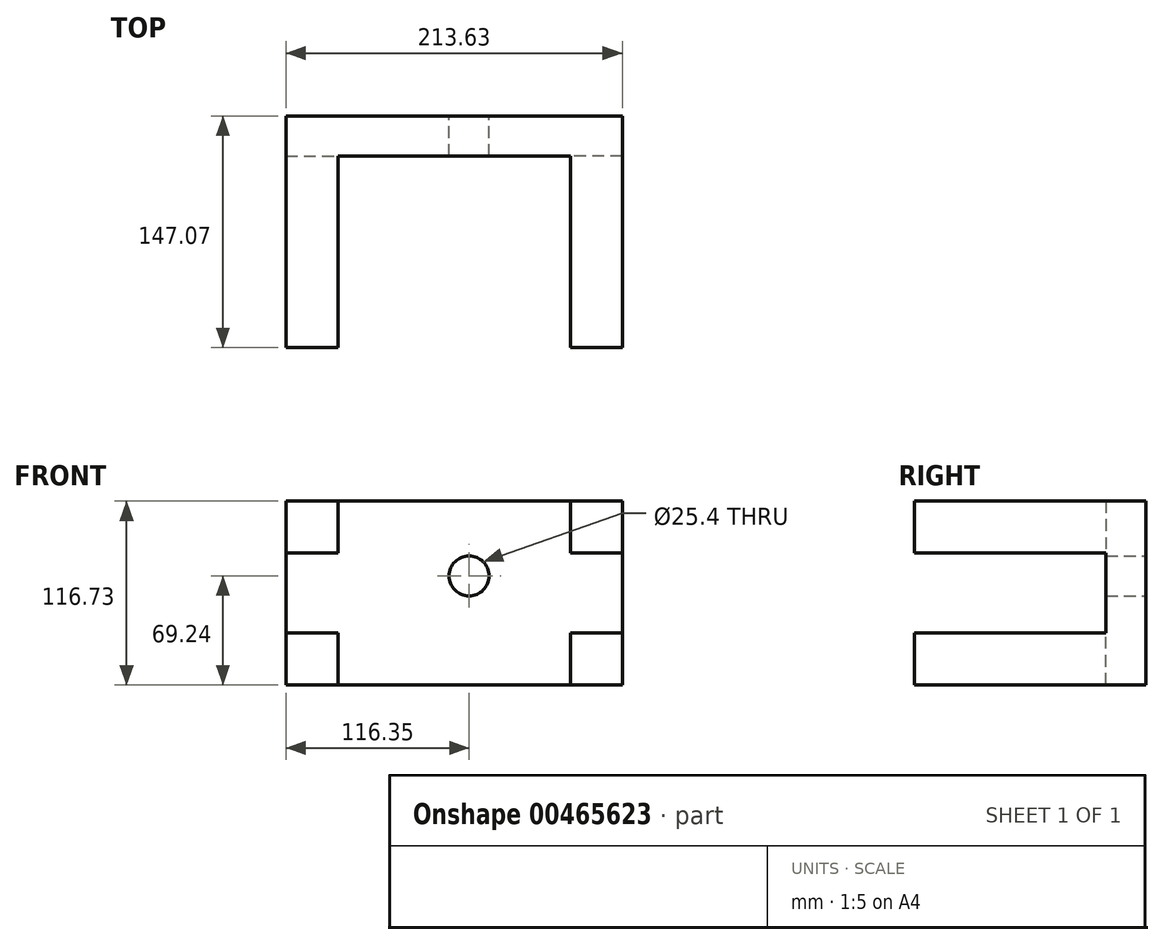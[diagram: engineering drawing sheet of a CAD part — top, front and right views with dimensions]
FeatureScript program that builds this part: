
annotation { "Feature Type Name" : "Feature", "Feature Type Description" : "" }
export const myFeature = defineFeature(function(context is Context, id is Id, definition is map)
    precondition{}
    {
        {
            var Q0;
            Q0=qCreatedBy(makeId("Front.planeOp"),FACE);
            var sketch = newSketch(context, id + "F0", { "sketchPlane" : qUnion([Q0])});
            skLineSegment(sketch, "E0.bottom", {"start": v(-116.35, 47.5) * mm, "end": v(97.28, 47.5) * mm});
            skLineSegment(sketch, "E0.top", {"start": v(-116.35, -69.24) * mm, "end": v(97.28, -69.24) * mm});
            skLineSegment(sketch, "E0.left", {"start": v(-116.35, 47.5) * mm, "end": v(-116.35, -69.24) * mm});
            skLineSegment(sketch, "E0.right", {"start": v(97.28, 47.5) * mm, "end": v(97.28, -69.24) * mm});
            skSolve(sketch);
        }
        {
            var Q0;
            Q0 = qSketchRegion(id + "F0", true);
            extrude(context, id + "F1", {"entities" : qUnion([Q0]), "depth" : 25.4 * mm});
        }
        {
            var Q0;
            Q0=makeQuery(id+"F1.opExtrude","CAP_FACE",FACE,{"disambiguationData":[OSD([sQuery(id+"F0.wireOp",EDGE,"E0.bottom"),sQuery(id+"F0.wireOp",EDGE,"E0.top"),sQuery(id+"F0.wireOp",EDGE,"E0.left"),sQuery(id+"F0.wireOp",EDGE,"E0.right")])],"isStart":false});
            var sketch = newSketch(context, id + "F2", { "sketchPlane" : qUnion([Q0])});
            skLineSegment(sketch, "E1.bottom", {"start": v(-116.35, 47.5) * mm, "end": v(-83.33, 47.5) * mm});
            skLineSegment(sketch, "E1.top", {"start": v(-116.35, 14.47) * mm, "end": v(-83.33, 14.47) * mm});
            skLineSegment(sketch, "E1.left", {"start": v(-116.35, 47.5) * mm, "end": v(-116.35, 14.47) * mm});
            skLineSegment(sketch, "E1.right", {"start": v(-83.33, 47.5) * mm, "end": v(-83.33, 14.47) * mm});
            skLineSegment(sketch, "E2.bottom", {"start": v(97.28, 47.5) * mm, "end": v(64.26, 47.5) * mm});
            skLineSegment(sketch, "E2.top", {"start": v(97.28, 14.47) * mm, "end": v(64.26, 14.47) * mm});
            skLineSegment(sketch, "E2.left", {"start": v(97.28, 47.5) * mm, "end": v(97.28, 14.47) * mm});
            skLineSegment(sketch, "E2.right", {"start": v(64.26, 47.5) * mm, "end": v(64.26, 14.47) * mm});
            skLineSegment(sketch, "E3.bottom", {"start": v(97.28, -69.24) * mm, "end": v(64.26, -69.24) * mm});
            skLineSegment(sketch, "E3.top", {"start": v(97.28, -36.22) * mm, "end": v(64.26, -36.22) * mm});
            skLineSegment(sketch, "E3.left", {"start": v(97.28, -69.24) * mm, "end": v(97.28, -36.22) * mm});
            skLineSegment(sketch, "E3.right", {"start": v(64.26, -69.24) * mm, "end": v(64.26, -36.22) * mm});
            skLineSegment(sketch, "E4.bottom", {"start": v(-116.35, -69.24) * mm, "end": v(-83.33, -69.24) * mm});
            skLineSegment(sketch, "E4.top", {"start": v(-116.35, -36.22) * mm, "end": v(-83.33, -36.22) * mm});
            skLineSegment(sketch, "E4.left", {"start": v(-116.35, -69.24) * mm, "end": v(-116.35, -36.22) * mm});
            skLineSegment(sketch, "E4.right", {"start": v(-83.33, -69.24) * mm, "end": v(-83.33, -36.22) * mm});
            skSolve(sketch);
        }
        {
            var Q0;
            Q0 = qSketchRegion(id + "F2", true);
            extrude(context, id + "F3", {"entities" : qUnion([Q0]), "operationType" : NewBodyOperationType.ADD, "depth" : 121.67 * mm});
        }
        {
            var Q0;
            Q0=makeQuery(id+"F1.opExtrude","CAP_FACE",FACE,{"disambiguationData":[OSD([sQuery(id+"F0.wireOp",EDGE,"E0.bottom"),sQuery(id+"F0.wireOp",EDGE,"E0.top"),sQuery(id+"F0.wireOp",EDGE,"E0.left"),sQuery(id+"F0.wireOp",EDGE,"E0.right")])],"isStart":true});
            var sketch = newSketch(context, id + "F4", { "sketchPlane" : qUnion([Q0])});
            skPoint(sketch, "E5", {"position": v(0, 0) * mm});
            skSolve(sketch);
        }
        {
            var Q0;
            Q0=sQuery(id+"F4.wireOp",VERTEX,"E5");
            var Q1;
            Q1=makeQuery(id+"F1.opExtrude","SWEPT_BODY",BODY,{"disambiguationData":[OSD([sQuery(id+"F0.wireOp",EDGE,"E0.bottom"),sQuery(id+"F0.wireOp",EDGE,"E0.top"),sQuery(id+"F0.wireOp",EDGE,"E0.left"),sQuery(id+"F0.wireOp",EDGE,"E0.right")])]});
            hole(context, id + "F5", {"style" : HoleStyle.SIMPLE, "endStyle" : HoleEndStyle.THROUGH, "holeDiameter" : 25.4 * mm, "isTappedThrough" : true, "tappedDepth" : 12.7 * mm, "tapClearance" : 3, "locations" : qUnion([Q0]), "scope" : qUnion([Q1])});
        }
    });
